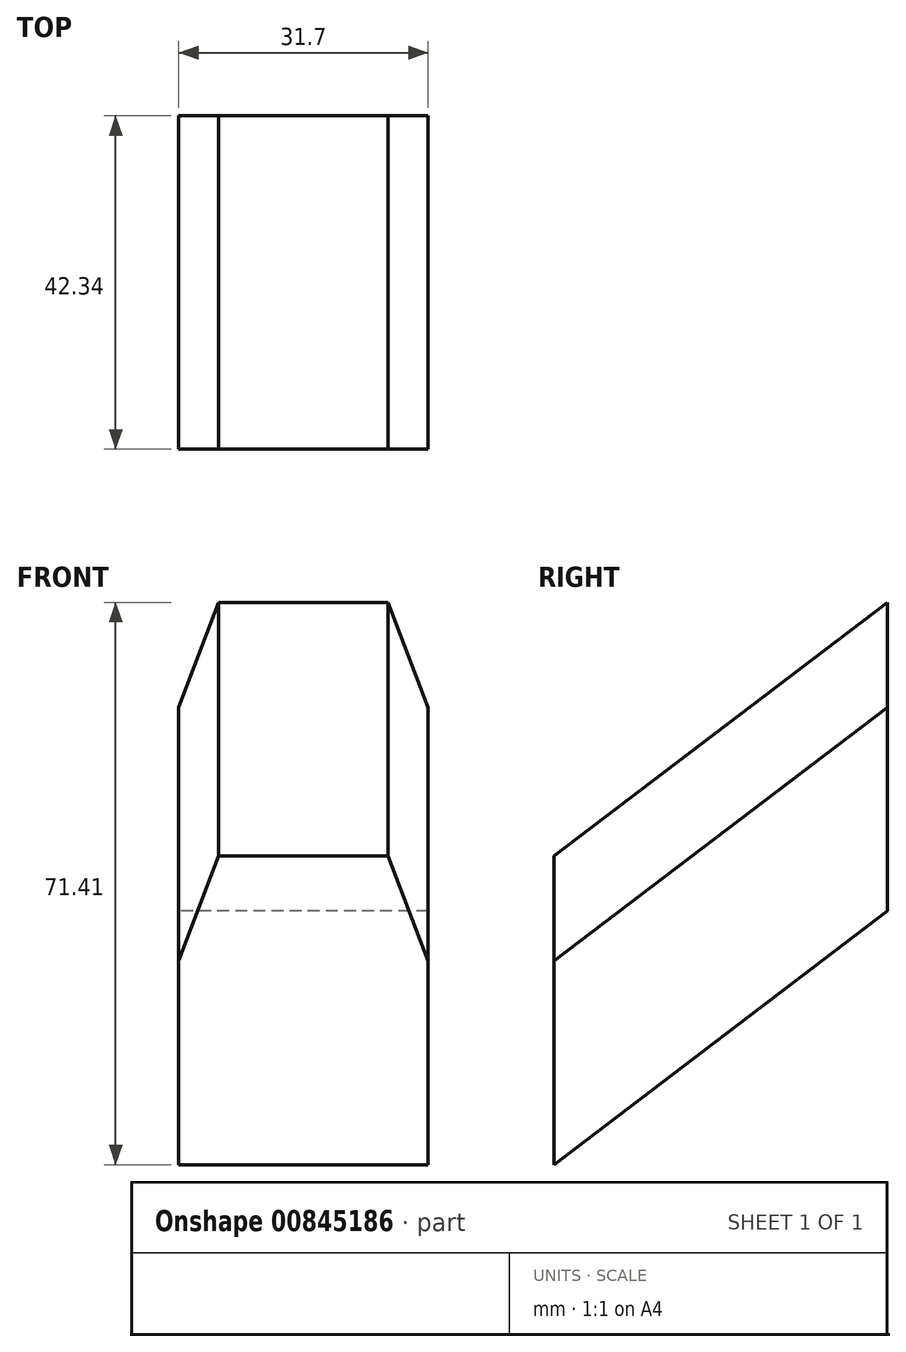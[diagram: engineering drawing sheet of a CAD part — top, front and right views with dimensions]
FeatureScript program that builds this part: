
annotation { "Feature Type Name" : "Feature", "Feature Type Description" : "" }
export const myFeature = defineFeature(function(context is Context, id is Id, definition is map)
    precondition{}
    {
        {
            var Q0;
            Q0=qCreatedBy(makeId("Front.planeOp"),FACE);
            var sketch = newSketch(context, id + "F0", { "sketchPlane" : qUnion([Q0])});
            skLineSegment(sketch, "E0.bottom", {"start": v(0, 0) * mm, "end": v(15.85, 0) * mm});
            skLineSegment(sketch, "E0.top", {"start": v(3.75, 39.2) * mm, "end": v(10.77, 39.2) * mm});
            skLineSegment(sketch, "E0.right", {"start": v(15.85, 0) * mm, "end": v(15.85, 25.89) * mm});
            skLineSegment(sketch, "E1", {"start": v(10.77, 39.2) * mm, "end": v(15.85, 25.89) * mm});
            skLineSegment(sketch, "E2.MirrorCS", {"start": v(-15.85, 0) * mm, "end": v(-15.85, 25.89) * mm});
            skLineSegment(sketch, "E3.MirrorCS", {"start": v(0, 0) * mm, "end": v(-15.85, 0) * mm});
            skLineSegment(sketch, "E4.MirrorCS", {"start": v(-10.77, 39.2) * mm, "end": v(-15.85, 25.89) * mm});
            skLineSegment(sketch, "E5.MirrorCS", {"start": v(-3.75, 39.2) * mm, "end": v(-10.77, 39.2) * mm});
            skLineSegment(sketch, "E6", {"start": v(3.75, 39.2) * mm, "end": v(-3.75, 39.2) * mm});
            skSolve(sketch);
        }
        {
            var Q0;
            Q0=qCreatedBy(makeId("Right.planeOp"),FACE);
            var sketch = newSketch(context, id + "F1", { "sketchPlane" : qUnion([Q0])});
            skLineSegment(sketch, "E7", {"start": v(0, 0) * mm, "end": v(42.34, 32.22) * mm});
            skSolve(sketch);
        }
        {
            var Q0;
            Q0=makeQuery(id+"F0.imprint","IMPRINT",FACE,{"disambiguationData":[TD([[makeQuery(id+"F0.imprint","IMPRINT",EDGE,{"derivedFrom":sQuery(id+"F0.wireOp",EDGE,"E0.bottom")}),1.0]])]});
            var Q1;
            Q1=sQuery(id+"F1.wireOp",EDGE,"E7");
            sweep(context, id + "F2", {"profiles" : qUnion([Q0]), "path" : qUnion([Q1])});
        }
    });
